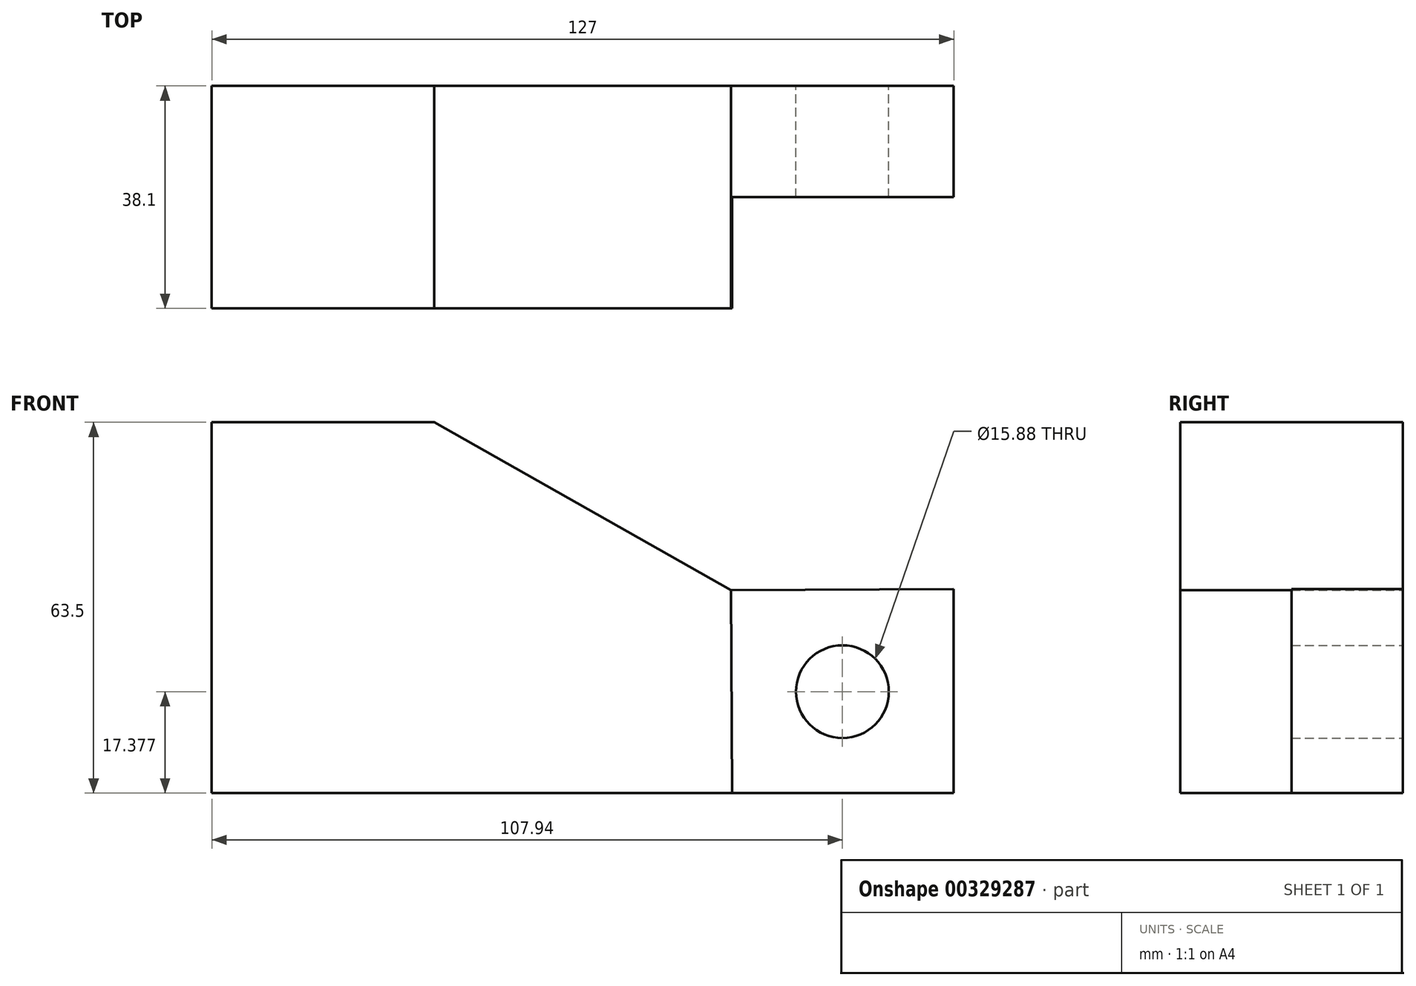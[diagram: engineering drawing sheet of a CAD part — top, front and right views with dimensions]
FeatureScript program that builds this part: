
annotation { "Feature Type Name" : "Feature", "Feature Type Description" : "" }
export const myFeature = defineFeature(function(context is Context, id is Id, definition is map)
    precondition{}
    {
        {
            var Q0;
            Q0=qCreatedBy(makeId("Front.planeOp"),FACE);
            var sketch = newSketch(context, id + "F0", { "sketchPlane" : qUnion([Q0])});
            skLineSegment(sketch, "E0", {"start": v(-83.1, -34.74) * mm, "end": v(43.9, -34.74) * mm});
            skLineSegment(sketch, "E1", {"start": v(-83.1, -34.74) * mm, "end": v(-83.1, 28.76) * mm});
            skLineSegment(sketch, "E2", {"start": v(43.9, -34.74) * mm, "end": v(43.9, 0.18) * mm});
            skLineSegment(sketch, "E3", {"start": v(43.9, 0.18) * mm, "end": v(5.8, 0) * mm});
            skLineSegment(sketch, "E4", {"start": v(-83.1, 28.76) * mm, "end": v(-45, 28.76) * mm});
            skLineSegment(sketch, "E5", {"start": v(-45, 28.76) * mm, "end": v(5.8, 0) * mm});
            skLineSegment(sketch, "E6", {"start": v(5.8, 0) * mm, "end": v(5.98, -34.74) * mm});
            skCircle(sketch, "E7", {"center": v(24.85, -17.36) * mm, "radius": 7.94 * mm});
            skSolve(sketch);
        }
        {
            var Q0;
            {var subQ0=sQuery(id+"F0.wireOp",EDGE,"E1");Q0=makeQuery(id+"F0.imprint","IMPRINT",FACE,{"disambiguationData":[TD([[makeQuery(id+"F0.imprint","IMPRINT",EDGE,{"derivedFrom":subQ0}),-1.0]])]});}
            extrude(context, id + "F1", {"entities" : qUnion([Q0]), "depth" : 38.1 * mm});
        }
        {
            var Q0;
            Q0 = qSketchRegion(id + "F0", true);
            extrude(context, id + "F2", {"entities" : qUnion([Q0]), "operationType" : NewBodyOperationType.ADD, "depth" : 19.05 * mm});
        }
    });
